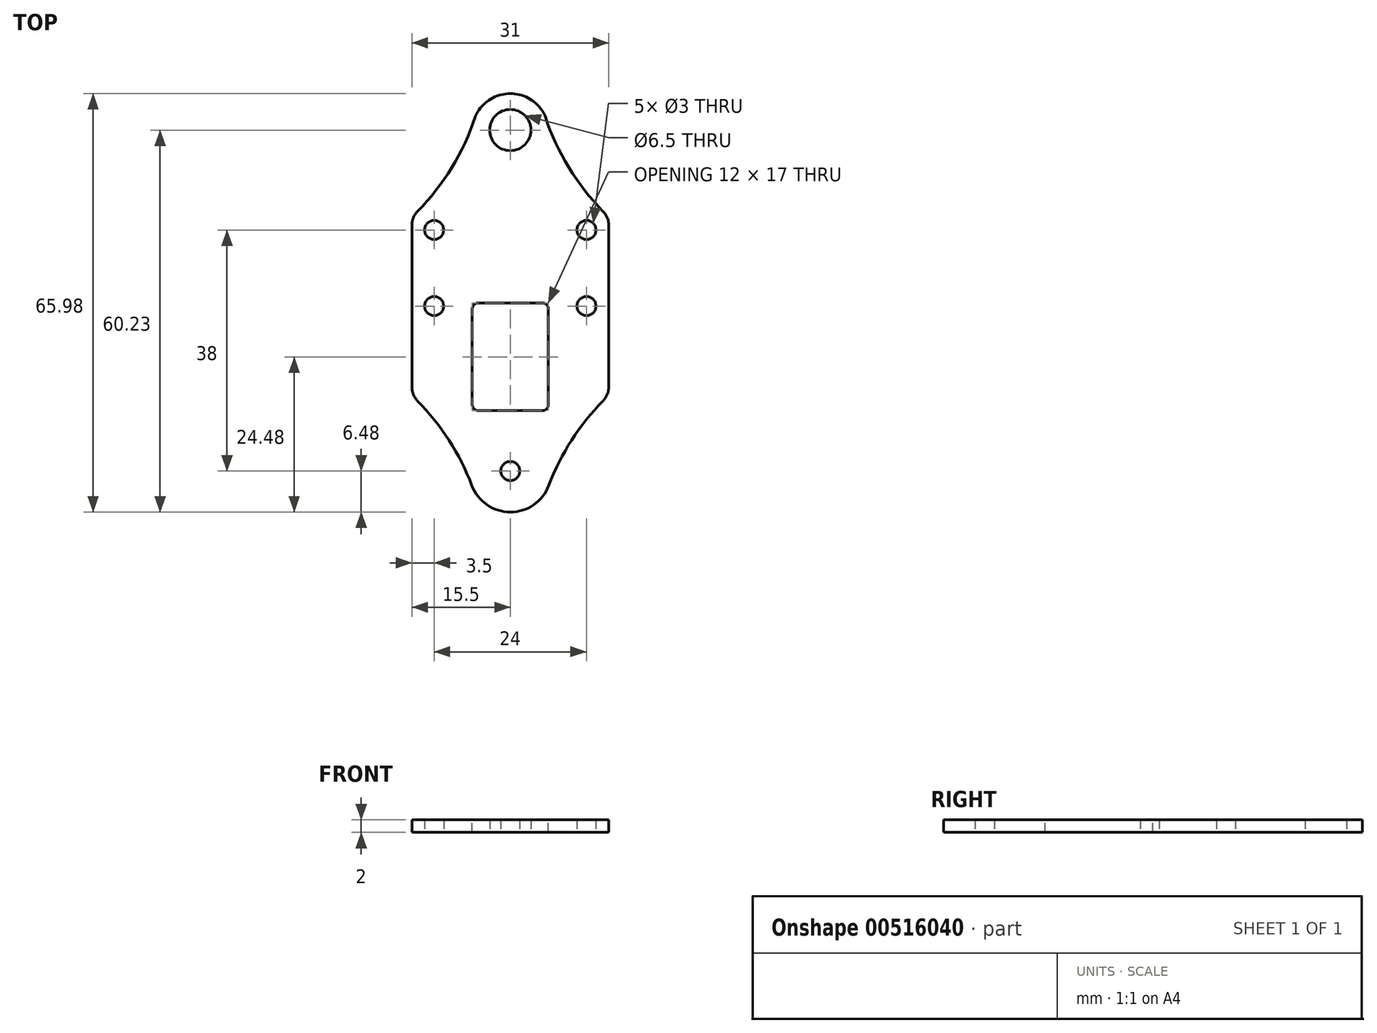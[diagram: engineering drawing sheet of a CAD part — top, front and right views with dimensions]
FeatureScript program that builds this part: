
annotation { "Feature Type Name" : "Feature", "Feature Type Description" : "" }
export const myFeature = defineFeature(function(context is Context, id is Id, definition is map)
    precondition{}
    {
        {
            var Q0;
            Q0=qCreatedBy(makeId("Top.planeOp"),FACE);
            var sketch = newSketch(context, id + "F0", { "sketchPlane" : qUnion([Q0])});
            skLineSegment(sketch, "E0", {"start": v(-15.5, 0) * mm, "end": v(15.5, 0) * mm, "construction": true});
            skLineSegment(sketch, "E1", {"start": v(0, -15.5) * mm, "end": v(0, 15.5) * mm, "construction": true});
            skLineSegment(sketch, "E2.top", {"start": v(-15.5, 15.5) * mm, "end": v(15.5, 15.5) * mm, "construction": true});
            skLineSegment(sketch, "E2.left", {"start": v(-15.5, -14.08) * mm, "end": v(-15.5, 14.08) * mm});
            skLineSegment(sketch, "E2.right", {"start": v(15.5, -14.08) * mm, "end": v(15.5, 14.08) * mm});
            skLineSegment(sketch, "E3", {"start": v(-15.5, -15.5) * mm, "end": v(15.5, 15.5) * mm, "construction": true});
            skLineSegment(sketch, "E4", {"start": v(-15.5, 15.5) * mm, "end": v(15.5, -15.5) * mm, "construction": true});
            skLineSegment(sketch, "E5", {"start": v(-12, -12) * mm, "end": v(12, -12) * mm, "construction": true});
            skLineSegment(sketch, "E6", {"start": v(12, -12) * mm, "end": v(12, 12) * mm, "construction": true});
            skLineSegment(sketch, "E7", {"start": v(12, 12) * mm, "end": v(-12, 12) * mm, "construction": true});
            skLineSegment(sketch, "E8", {"start": v(-12, 12) * mm, "end": v(-12, -12) * mm, "construction": true});
            skCircle(sketch, "E9", {"center": v(-12, -12) * mm, "radius": 1.5 * mm, "construction": true});
            skCircle(sketch, "E10", {"center": v(-12, 12) * mm, "radius": 1.5 * mm});
            skCircle(sketch, "E11", {"center": v(12, 12) * mm, "radius": 1.5 * mm});
            skCircle(sketch, "E12", {"center": v(12, -12) * mm, "radius": 1.5 * mm, "construction": true});
            skLineSegment(sketch, "E13", {"start": v(-5.38, 30.26) * mm, "end": v(-4.95, 30.9) * mm});
            skLineSegment(sketch, "E14", {"start": v(4.95, 30.9) * mm, "end": v(5.38, 30.26) * mm});
            skPoint(sketch, "E15.visualSharp", {"position": v(0, 38.11) * mm});
            skArc(sketch, "E15.filletArc", {"start": v(4.95, 30.9) * mm, "mid": v(0, 33.5) * mm, "end": v(-4.95, 30.9) * mm});
            skCircle(sketch, "E16", {"center": v(0, 27.75) * mm, "radius": 3.25 * mm});
            skCircle(sketch, "E17", {"center": v(0, 0) * mm, "radius": 59 * mm, "construction": true});
            skLineSegment(sketch, "E18", {"start": v(0, 0) * mm, "end": v(-41.72, -41.72) * mm, "construction": true});
            skCircle(sketch, "E19", {"center": v(-41.72, -41.72) * mm, "radius": 38.1 * mm, "construction": true});
            skArc(sketch, "E20", {"start": v(-6.07, -28.29) * mm, "mid": v(0, -32.48) * mm, "end": v(6.07, -28.29) * mm});
            skArc(sketch, "E21", {"start": v(-6.07, -28.29) * mm, "mid": v(-9.98, -20.65) * mm, "end": v(-15.5, -14.08) * mm});
            skArc(sketch, "E22", {"start": v(6.07, -28.29) * mm, "mid": v(9.98, -20.65) * mm, "end": v(15.5, -14.08) * mm});
            skCircle(sketch, "E23", {"center": v(0, -26) * mm, "radius": 1.5 * mm});
            skCircle(sketch, "E24", {"center": v(-12, 0) * mm, "radius": 1.5 * mm});
            skCircle(sketch, "E25", {"center": v(12, 0) * mm, "radius": 1.5 * mm});
            skArc(sketch, "E26", {"start": v(-15.5, 14.08) * mm, "mid": v(-9.41, 21.52) * mm, "end": v(-5.38, 30.26) * mm});
            skArc(sketch, "E27", {"start": v(15.5, 14.08) * mm, "mid": v(9.41, 21.52) * mm, "end": v(5.38, 30.26) * mm});
            skSolve(sketch);
        }
        {
            var Q0;
            Q0=qSketchRegion(id+"F0",true);
            extrude(context, id + "F1", {"entities" : qUnion([Q0]), "depth" : 2 * mm, "offsetDistance" : 25 * mm});
        }
        {
            var Q0;
            Q0=makeQuery(id+"F1.opExtrude","SWEPT_EDGE",EDGE,{"disambiguationData":[OSD([sQuery(id+"F0.wireOp",EDGE,"E2.bottom"),sQuery(id+"F0.wireOp",EDGE,"E2.left")])]});
            var Q1;
            Q1=makeQuery(id+"F1.opExtrude","SWEPT_EDGE",EDGE,{"disambiguationData":[OSD([sQuery(id+"F0.wireOp",EDGE,"E2.bottom"),sQuery(id+"F0.wireOp",EDGE,"E2.right")])]});
            var Q2;
            Q2=makeQuery(id+"F1.opExtrude","SWEPT_EDGE",EDGE,{"disambiguationData":[OSD([sQuery(id+"F0.wireOp",EDGE,"E2.top"),sQuery(id+"F0.wireOp",EDGE,"E2.left")])]});
            var Q3;
            Q3=makeQuery(id+"F1.opExtrude","SWEPT_EDGE",EDGE,{"disambiguationData":[OSD([sQuery(id+"F0.wireOp",EDGE,"E2.top"),sQuery(id+"F0.wireOp",EDGE,"E2.right")])]});
            var Q4;
            Q4=makeQuery(id+"F1.opExtrude","SWEPT_EDGE",EDGE,{"disambiguationData":[OSD([sQuery(id+"F0.wireOp",EDGE,"E14"),sQuery(id+"F0.wireOp",EDGE,"E27")])]});
            var Q5;
            Q5=makeQuery(id+"F1.opExtrude","SWEPT_EDGE",EDGE,{"disambiguationData":[OSD([sQuery(id+"F0.wireOp",EDGE,"E13"),sQuery(id+"F0.wireOp",EDGE,"E26")])]});
            fillet(context, id + "F2", {"entities" : qUnion([Q0, Q1, Q2, Q3, Q4, Q5]), "radius" : 3 * mm, "tangentPropagation" : true, "allowEdgeOverflow" : false});
        }
        {
            var Q0;
            Q0=makeQuery(id+"F1.opExtrude","CAP_FACE",FACE,{"disambiguationData":[OSD([sQuery(id+"F0.wireOp",EDGE,"E2.bottom"),sQuery(id+"F0.wireOp",EDGE,"E2.left"),sQuery(id+"F0.wireOp",EDGE,"E2.right"),sQuery(id+"F0.wireOp",EDGE,"E9"),sQuery(id+"F0.wireOp",EDGE,"E10"),sQuery(id+"F0.wireOp",EDGE,"E11"),sQuery(id+"F0.wireOp",EDGE,"E12"),sQuery(id+"F0.wireOp",EDGE,"E13"),sQuery(id+"F0.wireOp",EDGE,"E14"),sQuery(id+"F0.wireOp",EDGE,"E15.filletArc"),sQuery(id+"F0.wireOp",EDGE,"E16")])],"isStart":false});
            var sketch = newSketch(context, id + "F3", { "sketchPlane" : qUnion([Q0])});
            skLineSegment(sketch, "E28.bottom", {"start": v(-6, -16.5) * mm, "end": v(6, -16.5) * mm});
            skLineSegment(sketch, "E28.top", {"start": v(-6, 0.5) * mm, "end": v(6, 0.5) * mm});
            skLineSegment(sketch, "E28.left", {"start": v(-6, -16.5) * mm, "end": v(-6, 0.5) * mm});
            skLineSegment(sketch, "E28.right", {"start": v(6, -16.5) * mm, "end": v(6, 0.5) * mm});
            skSolve(sketch);
        }
        {
            var Q0;
            Q0 = qSketchRegion(id + "F3", true);
            extrude(context, id + "F4", {"entities" : qUnion([Q0]), "operationType" : NewBodyOperationType.REMOVE, "oppositeDirection" : true, "depth" : 25 * mm, "offsetDistance" : 25 * mm});
        }
        {
            var Q0;
            Q0=makeQuery(id+"F4.boolean.opBoolean","COPY",EDGE,{"derivedFrom":makeQuery(id+"F4.opExtrude","SWEPT_EDGE",EDGE,{"disambiguationData":[OSD([sQuery(id+"F3.wireOp",EDGE,"E28.top"),sQuery(id+"F3.wireOp",EDGE,"E28.left")])]})});
            var Q1;
            Q1=makeQuery(id+"F4.boolean.opBoolean","COPY",EDGE,{"derivedFrom":makeQuery(id+"F4.opExtrude","SWEPT_EDGE",EDGE,{"disambiguationData":[OSD([sQuery(id+"F3.wireOp",EDGE,"E28.top"),sQuery(id+"F3.wireOp",EDGE,"E28.right")])]})});
            var Q2;
            Q2=makeQuery(id+"F4.boolean.opBoolean","COPY",EDGE,{"derivedFrom":makeQuery(id+"F4.opExtrude","SWEPT_EDGE",EDGE,{"disambiguationData":[OSD([sQuery(id+"F3.wireOp",EDGE,"E28.bottom"),sQuery(id+"F3.wireOp",EDGE,"E28.right")])]})});
            var Q3;
            Q3=makeQuery(id+"F4.boolean.opBoolean","COPY",EDGE,{"derivedFrom":makeQuery(id+"F4.opExtrude","SWEPT_EDGE",EDGE,{"disambiguationData":[OSD([sQuery(id+"F3.wireOp",EDGE,"E28.bottom"),sQuery(id+"F3.wireOp",EDGE,"E28.left")])]})});
            fillet(context, id + "F5", {"entities" : qUnion([Q0, Q1, Q2, Q3]), "radius" : 1 * mm, "tangentPropagation" : true, "allowEdgeOverflow" : false});
        }
    });
